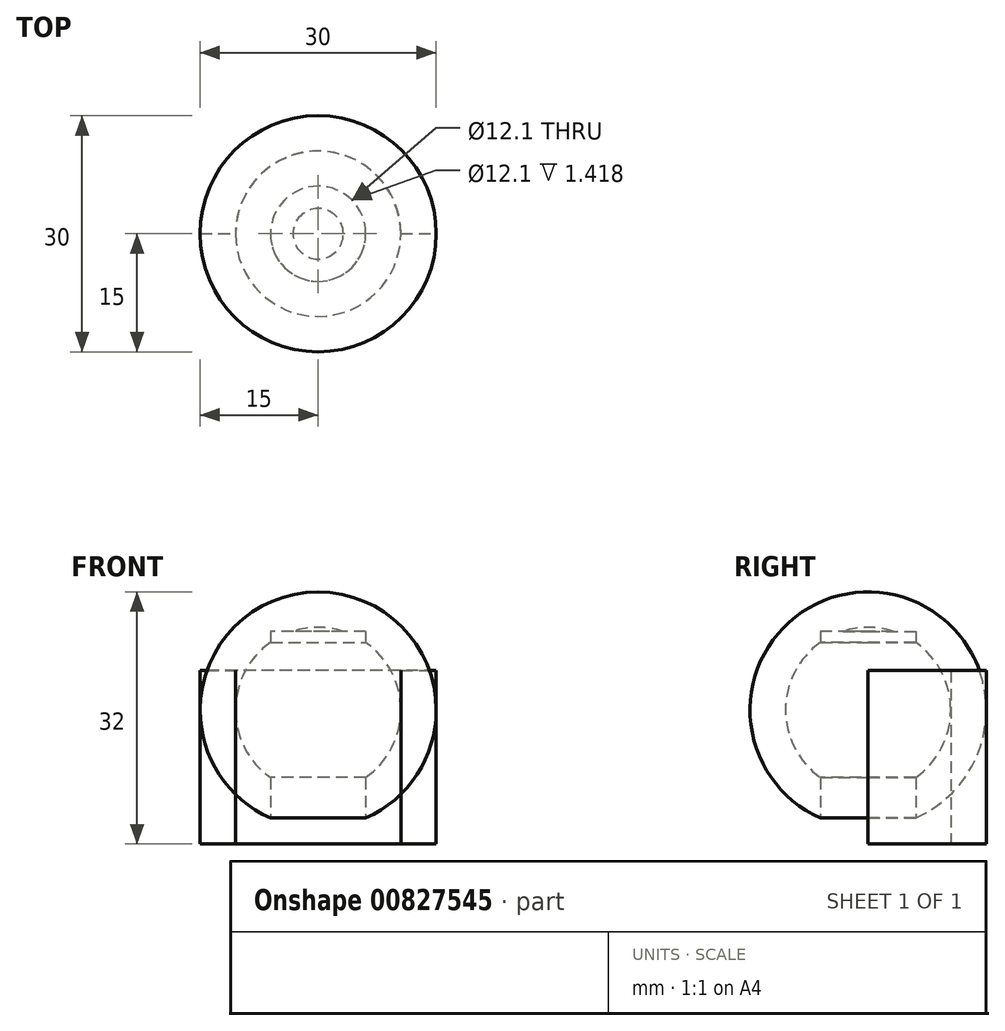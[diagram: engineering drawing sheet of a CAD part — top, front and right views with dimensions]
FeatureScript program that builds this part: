
annotation { "Feature Type Name" : "Feature", "Feature Type Description" : "" }
export const myFeature = defineFeature(function(context is Context, id is Id, definition is map)
    precondition{}
    {
        {
            var Q0;
            Q0=qCreatedBy(makeId("Top.planeOp"),FACE);
            var sketch = newSketch(context, id + "F0", { "sketchPlane" : qUnion([Q0])});
            skArc(sketch, "E0", {"start": v(15, 0) * mm, "mid": v(0, 15) * mm, "end": v(-15, 0) * mm});
            skLineSegment(sketch, "E1", {"start": v(-15, 0) * mm, "end": v(15, 0) * mm});
            skCircle(sketch, "E2", {"center": v(0, 0) * mm, "radius": 10.5 * mm});
            skCircle(sketch, "E3", {"center": v(0, 0) * mm, "radius": 6.05 * mm});
            skSolve(sketch);
        }
        {
            var Q0;
            {var subQ0=sQuery(id+"F0.wireOp",EDGE,"E2");var subQ1=sQuery(id+"F0.wireOp",EDGE,"E1");var subQ2=makeQuery(id+"F0.imprint","INTERSECT",VERTEX,{"disambiguationData":[OD(0.0)],"derivedFrom":[subQ1,subQ0]});Q0=makeQuery(id+"F0.imprint","IMPRINT",FACE,{"disambiguationData":[TD([[makeQuery(id+"F0.imprint","IMPRINT",EDGE,{"disambiguationData":[TD([[subQ2,-1.0]])],"derivedFrom":subQ1}),1.0]])]});}
            var Q1;
            {var subQ0=sQuery(id+"F0.wireOp",EDGE,"E2");var subQ1=sQuery(id+"F0.wireOp",EDGE,"E1");var subQ2=makeQuery(id+"F0.imprint","INTERSECT",VERTEX,{"disambiguationData":[OD(0.0)],"derivedFrom":[subQ1,subQ0]});Q1=makeQuery(id+"F0.imprint","IMPRINT",FACE,{"disambiguationData":[TD([[makeQuery(id+"F0.imprint","IMPRINT",EDGE,{"disambiguationData":[TD([[subQ2,-1.0]])],"derivedFrom":subQ1}),-1.0]])]});}
            extrude(context, id + "F1", {"entities" : qUnion([Q0, Q1]), "depth" : 5 * mm, "offsetDistance" : 25.4 * mm, "hasSecondDirection" : true, "secondDirectionOppositeDirection" : true, "secondDirectionDepth" : 17 * mm});
        }
        {
            var Q0;
            {var subQ0=sQuery(id+"F0.wireOp",EDGE,"E3");var subQ1=sQuery(id+"F0.wireOp",EDGE,"E1");var subQ2=makeQuery(id+"F0.imprint","INTERSECT",VERTEX,{"disambiguationData":[OD(0.0)],"derivedFrom":[subQ1,subQ0]});Q0=makeQuery(id+"F0.imprint","IMPRINT",FACE,{"disambiguationData":[TD([[makeQuery(id+"F0.imprint","IMPRINT",EDGE,{"disambiguationData":[TD([[subQ2,-1.0]])],"derivedFrom":subQ1}),1.0]])]});}
            var Q1;
            {var subQ0=sQuery(id+"F0.wireOp",EDGE,"E3");var subQ1=sQuery(id+"F0.wireOp",EDGE,"E1");var subQ2=makeQuery(id+"F0.imprint","INTERSECT",VERTEX,{"disambiguationData":[OD(0.0)],"derivedFrom":[subQ1,subQ0]});Q1=makeQuery(id+"F0.imprint","IMPRINT",FACE,{"disambiguationData":[TD([[makeQuery(id+"F0.imprint","IMPRINT",EDGE,{"disambiguationData":[TD([[subQ2,-1.0]])],"derivedFrom":subQ1}),-1.0]])]});}
            extrude(context, id + "F2", {"entities" : qUnion([Q0, Q1]), "depth" : 10 * mm, "offsetDistance" : 25.4 * mm, "hasSecondDirection" : true, "secondDirectionOppositeDirection" : true, "secondDirectionDepth" : 25 * mm});
        }
        {
            var Q0;
            Q0=makeQuery(id+"F0.imprint","IMPRINT",FACE,{"disambiguationData":[TD([[makeQuery(id+"F0.imprint","IMPRINT",EDGE,{"derivedFrom":sQuery(id+"F0.wireOp",EDGE,"E0")}),1.0]])]});
            var Q1;
            Q1=sQuery(id+"F0.wireOp",EDGE,"E1");
            revolve(context, id + "F3", {"surfaceOperationType" : NewSurfaceOperationType.NEW, "entities" : qUnion([Q0]), "axis" : qUnion([Q1]), "revolveType" : RevolveType.FULL});
        }
        {
            var Q0;
            Q0=makeQuery(id+"F2.opExtrude","SWEPT_BODY",BODY,{"disambiguationData":[OSD([sQuery(id+"F0.wireOp",EDGE,"E3")])]});
            var Q1;
            Q1=makeQuery(id+"F1.opExtrude","SWEPT_BODY",BODY,{"disambiguationData":[OSD([sQuery(id+"F0.wireOp",EDGE,"E2"),sQuery(id+"F0.wireOp",EDGE,"E3")])]});
            var Q2;
            Q2=makeQuery(id+"F3.opRevolve","SWEPT_BODY",BODY,{"disambiguationData":[OSD([sQuery(id+"F0.wireOp",EDGE,"E0"),sQuery(id+"F0.wireOp",EDGE,"E1"),sQuery(id+"F0.wireOp",EDGE,"E2")])]});
            booleanBodies(context, id + "F4", {"operationType" : BooleanOperationType.SUBTRACTION, "tools" : qUnion([Q0]), "targets" : qUnion([Q1, Q2])});
        }
    });
